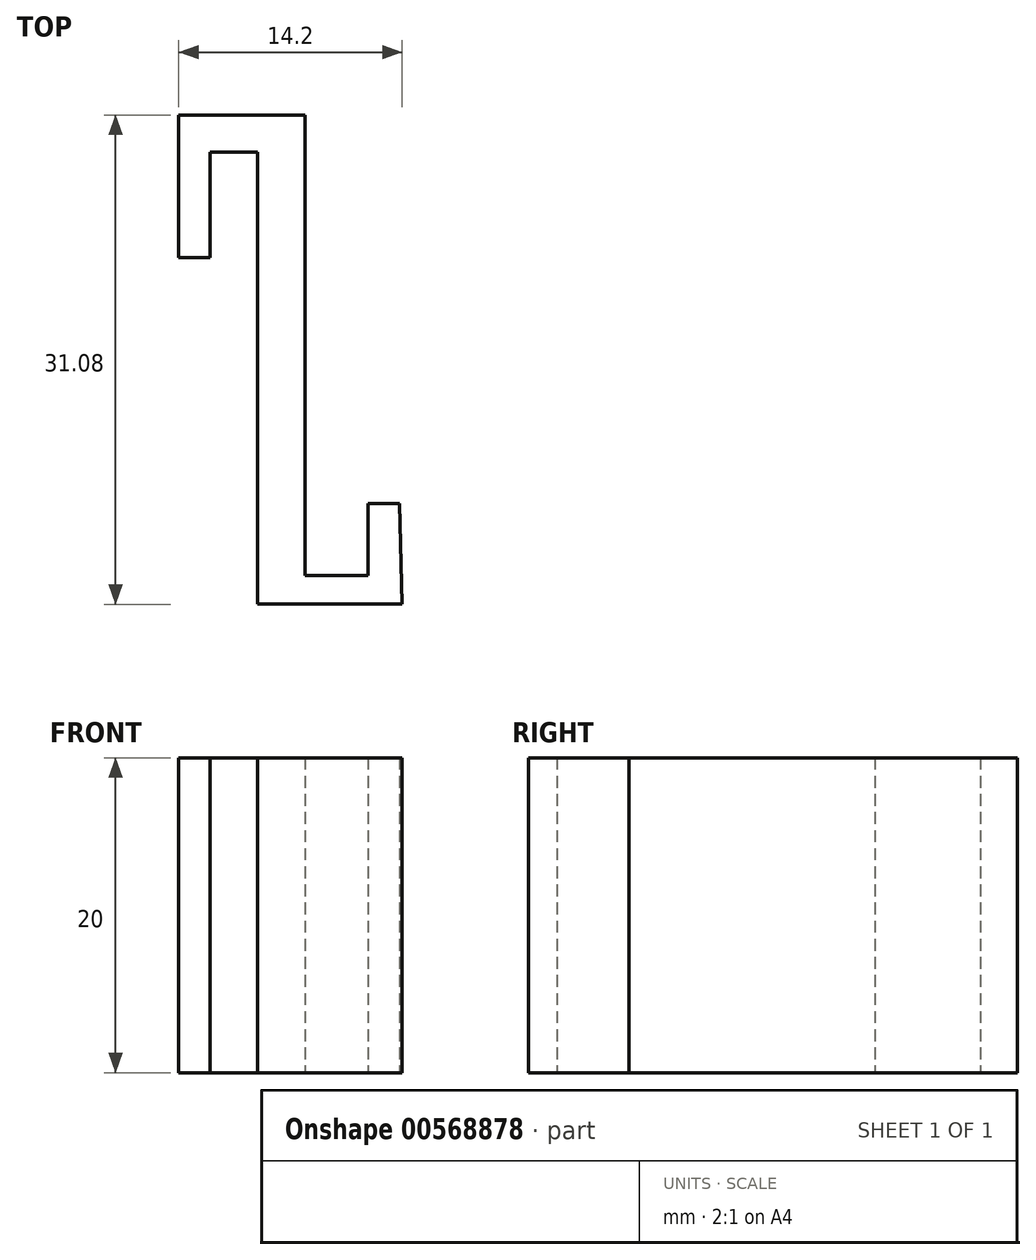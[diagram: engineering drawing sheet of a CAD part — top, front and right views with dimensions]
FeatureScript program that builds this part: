
annotation { "Feature Type Name" : "Feature", "Feature Type Description" : "" }
export const myFeature = defineFeature(function(context is Context, id is Id, definition is map)
    precondition{}
    {
        {
            var Q0;
            Q0=qCreatedBy(makeId("Front.planeOp"),FACE);
            var sketch = newSketch(context, id + "F0", { "sketchPlane" : qUnion([Q0])});
            skLineSegment(sketch, "E0", {"start": v(-7.04, 6.72) * mm, "end": v(-7.04, -22) * mm});
            skLineSegment(sketch, "E1", {"start": v(0, -22) * mm, "end": v(-7.04, -22) * mm});
            skLineSegment(sketch, "E2", {"start": v(-7.04, 6.72) * mm, "end": v(-10.04, 6.72) * mm});
            skLineSegment(sketch, "E3", {"start": v(-10.04, 6.72) * mm, "end": v(-10.04, 0) * mm});
            skLineSegment(sketch, "E4", {"start": v(-10.04, 0) * mm, "end": v(-12.04, 0) * mm});
            skLineSegment(sketch, "E5", {"start": v(-12.04, 0) * mm, "end": v(-12.04, 9.07) * mm});
            skLineSegment(sketch, "E6", {"start": v(-12.04, 9.07) * mm, "end": v(-4, 9.07) * mm});
            skLineSegment(sketch, "E7", {"start": v(-4, 9.07) * mm, "end": v(-4, -20.2) * mm});
            skLineSegment(sketch, "E8", {"start": v(-4, -20.2) * mm, "end": v(0, -20.2) * mm});
            skLineSegment(sketch, "E9", {"start": v(0, -20.2) * mm, "end": v(0, -15.6) * mm});
            skLineSegment(sketch, "E10", {"start": v(0, -15.6) * mm, "end": v(2, -15.6) * mm});
            skLineSegment(sketch, "E11", {"start": v(2, -15.6) * mm, "end": v(2.16, -22) * mm});
            skLineSegment(sketch, "E12", {"start": v(2.16, -22) * mm, "end": v(0, -22) * mm});
            skSolve(sketch);
        }
        {
            var Q0;
            Q0 = qSketchRegion(id + "F0", true);
            extrude(context, id + "F1", {"entities" : qUnion([Q0]), "depth" : 20 * mm, "offsetDistance" : 25 * mm});
        }
        {
            var Q0;
            Q0=makeQuery(id+"F1.opExtrude","SWEPT_BODY",BODY,{"disambiguationData":[OSD([sQuery(id+"F0.wireOp",EDGE,"E0"),sQuery(id+"F0.wireOp",EDGE,"E1"),sQuery(id+"F0.wireOp",EDGE,"E2"),sQuery(id+"F0.wireOp",EDGE,"E3"),sQuery(id+"F0.wireOp",EDGE,"E4"),sQuery(id+"F0.wireOp",EDGE,"E5"),sQuery(id+"F0.wireOp",EDGE,"E6"),sQuery(id+"F0.wireOp",EDGE,"E7"),sQuery(id+"F0.wireOp",EDGE,"E8"),sQuery(id+"F0.wireOp",EDGE,"E9"),sQuery(id+"F0.wireOp",EDGE,"E10"),sQuery(id+"F0.wireOp",EDGE,"E11"),sQuery(id+"F0.wireOp",EDGE,"E12")])]});
            var Q1;
            Q1=makeQuery(id+"F1.opExtrude","CAP_EDGE",EDGE,{"disambiguationData":[OSD([sQuery(id+"F0.wireOp",EDGE,"E8")])],"isStart":false});
            transform(context, id + "F2", {"entities" : qUnion([Q0]), "transformType" : TransformType.ROTATION, "transformAxis" : qUnion([Q1]), "angle" : 90 * degree, "oppositeDirection" : true, "makeCopy" : false});
        }
    });
